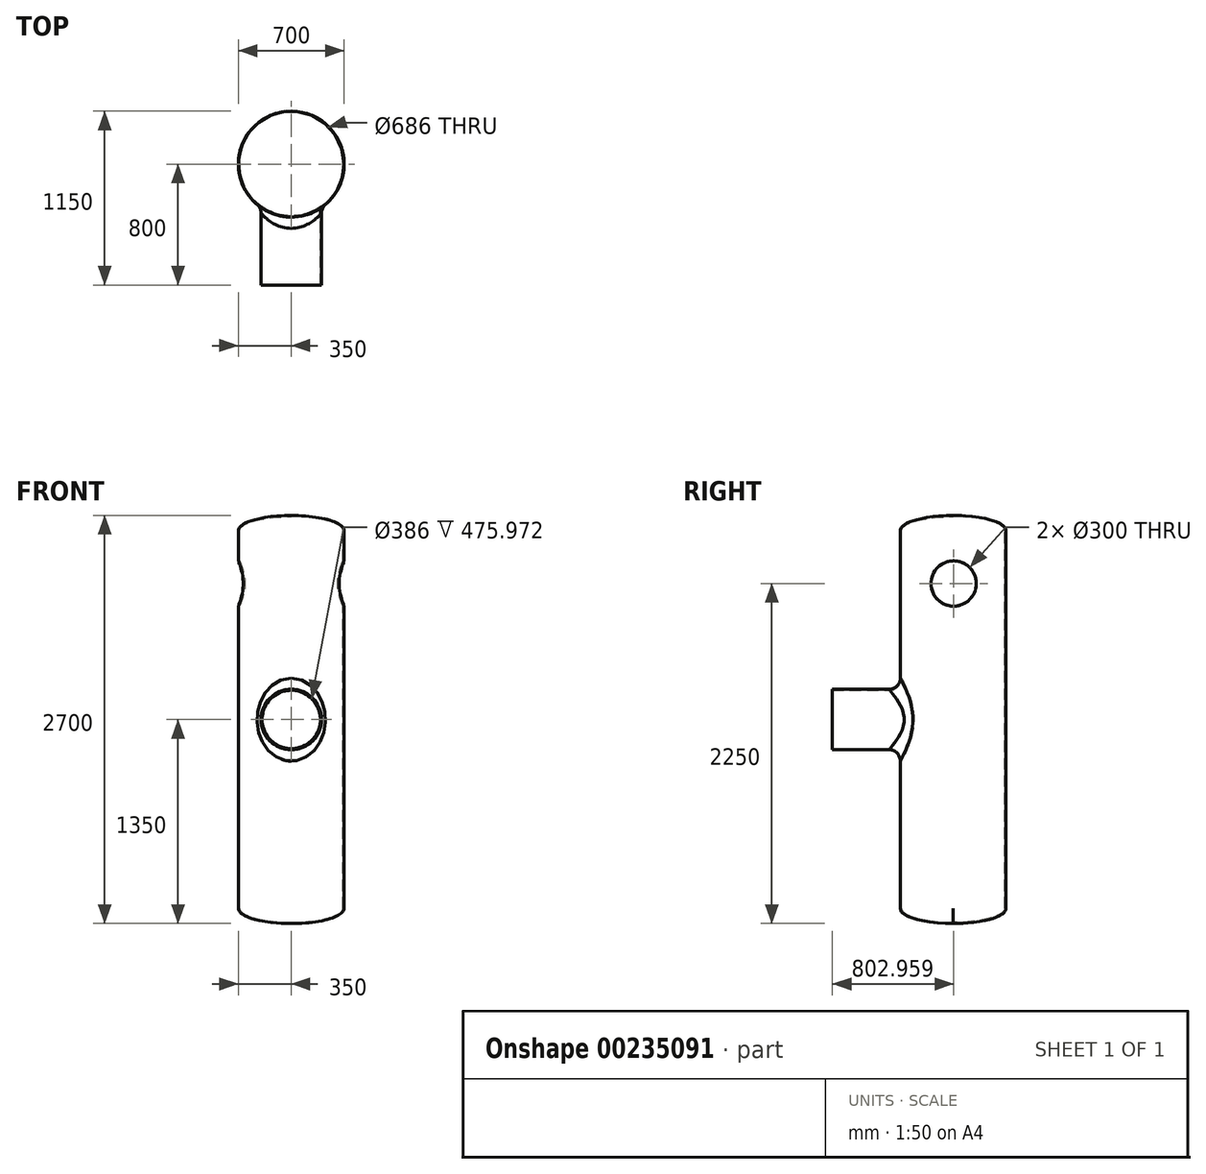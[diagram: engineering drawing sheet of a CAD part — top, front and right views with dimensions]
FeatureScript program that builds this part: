
annotation { "Feature Type Name" : "Feature", "Feature Type Description" : "" }
export const myFeature = defineFeature(function(context is Context, id is Id, definition is map)
    precondition{}
    {
        {
            var Q0;
            Q0=qCreatedBy(makeId("Front.planeOp"),FACE);
            var sketch = newSketch(context, id + "F0", { "sketchPlane" : qUnion([Q0])});
            skLineSegment(sketch, "E0.left", {"start": v(0, 0) * mm, "end": v(0, -2600) * mm});
            skLineSegment(sketch, "E0.right", {"start": v(350, 0) * mm, "end": v(350, -2500) * mm});
            skEllipticalArc(sketch, "E1", {});
            skLineSegment(sketch, "E2", {"start": v(0, 0) * mm, "end": v(0, 100) * mm});
            skPoint(sketch, "E2.endSnap0", {"position": v(0, 100) * mm});
            skPoint(sketch, "E3.start.orphan", {"position": v(350, -1250) * mm});
            skEllipticalArc(sketch, "E4.MirrorCS", {});
            const initialGuessF0  = {"E1": [0, 0, 0, 1, 0.1, 0.35, 4.71238898038469, 6.283185307179586], "E4.MirrorCS": [0, -2.5, 0, -1, 0.1, 0.35, 6.283185307179586, 1.5707963267948966]};
            skSetInitialGuess(sketch, initialGuessF0);
            skSolve(sketch);
        }
        {
            var Q0;
            Q0=makeQuery(id+"F0.imprint","IMPRINT",FACE,{"disambiguationData":[TD([[makeQuery(id+"F0.imprint","IMPRINT",EDGE,{"derivedFrom":sQuery(id+"F0.wireOp",EDGE,"E0.left")}),1.0]])]});
            var Q1;
            Q1=sQuery(id+"F0.wireOp",EDGE,"E0.left");
            revolve(context, id + "F1", {"entities" : qUnion([Q0]), "axis" : qUnion([Q1]), "revolveType" : RevolveType.FULL});
        }
        {
            var Q0;
            Q0=qCreatedBy(makeId("Front.planeOp"),FACE);
            var sketch = newSketch(context, id + "F2", { "sketchPlane" : qUnion([Q0])});
            skCircle(sketch, "E5", {"center": v(0, -1250) * mm, "radius": 200 * mm});
            skLineSegment(sketch, "E6.0", {"start": v(-350, 0) * mm, "end": v(350, 0) * mm});
            skSolve(sketch);
        }
        {
            var Q0;
            Q0 = qSketchRegion(id + "F2", true);
            extrude(context, id + "F3", {"entities" : qUnion([Q0]), "depth" : 800 * mm});
        }
        {
            var Q0;
            Q0=makeQuery(id+"F1.opRevolve","SWEPT_BODY",BODY,{"disambiguationData":[OSD([sQuery(id+"F0.wireOp",EDGE,"E0.left"),sQuery(id+"F0.wireOp",EDGE,"E0.right"),sQuery(id+"F0.wireOp",EDGE,"E1"),sQuery(id+"F0.wireOp",EDGE,"E2"),sQuery(id+"F0.wireOp",EDGE,"E4.MirrorCS")])]});
            var Q1;
            Q1=makeQuery(id+"F3.opExtrude","SWEPT_BODY",BODY,{"disambiguationData":[OSD([sQuery(id+"F2.wireOp",EDGE,"E5")])]});
            booleanBodies(context, id + "F4", {"operationType" : BooleanOperationType.UNION, "tools" : qUnion([Q0, Q1])});
        }
        {
            var Q0;
            Q0=makeQuery(id+"F4.opBoolean","INTERSECT",EDGE,{"derivedFrom":[makeQuery(id+"F1.opRevolve","SWEPT_FACE",FACE,{"disambiguationData":[OSD([sQuery(id+"F0.wireOp",EDGE,"E0.right")])]}),makeQuery(id+"F3.opExtrude","SWEPT_FACE",FACE,{"disambiguationData":[OSD([sQuery(id+"F2.wireOp",EDGE,"E5")])]})]});
            fillet(context, id + "F5", {"entities" : qUnion([Q0]), "radius" : 75 * mm, "tangentPropagation" : true, "allowEdgeOverflow" : false});
        }
        {
            var Q0;
            Q0=makeQuery(id+"F3.opExtrude","CAP_FACE",FACE,{"disambiguationData":[OSD([sQuery(id+"F2.wireOp",EDGE,"E5")])],"isStart":false});
            shell(context, id + "F6", {"entities" : qUnion([Q0]), "thickness" : 7 * mm});
        }
        {
            var Q0;
            Q0=qCreatedBy(makeId("Right.planeOp"),FACE);
            var sketch = newSketch(context, id + "F7", { "sketchPlane" : qUnion([Q0])});
            skCircle(sketch, "E7", {"center": v(2.96, -350) * mm, "radius": 150 * mm});
            skSolve(sketch);
        }
        {
            var Q0;
            Q0 = qSketchRegion(id + "F7", true);
            extrude(context, id + "F8", {"entities" : qUnion([Q0]), "operationType" : NewBodyOperationType.REMOVE, "endBound" : BoundingType.SYMMETRIC, "oppositeDirection" : true, "depth" : 2000 * mm});
        }
    });
